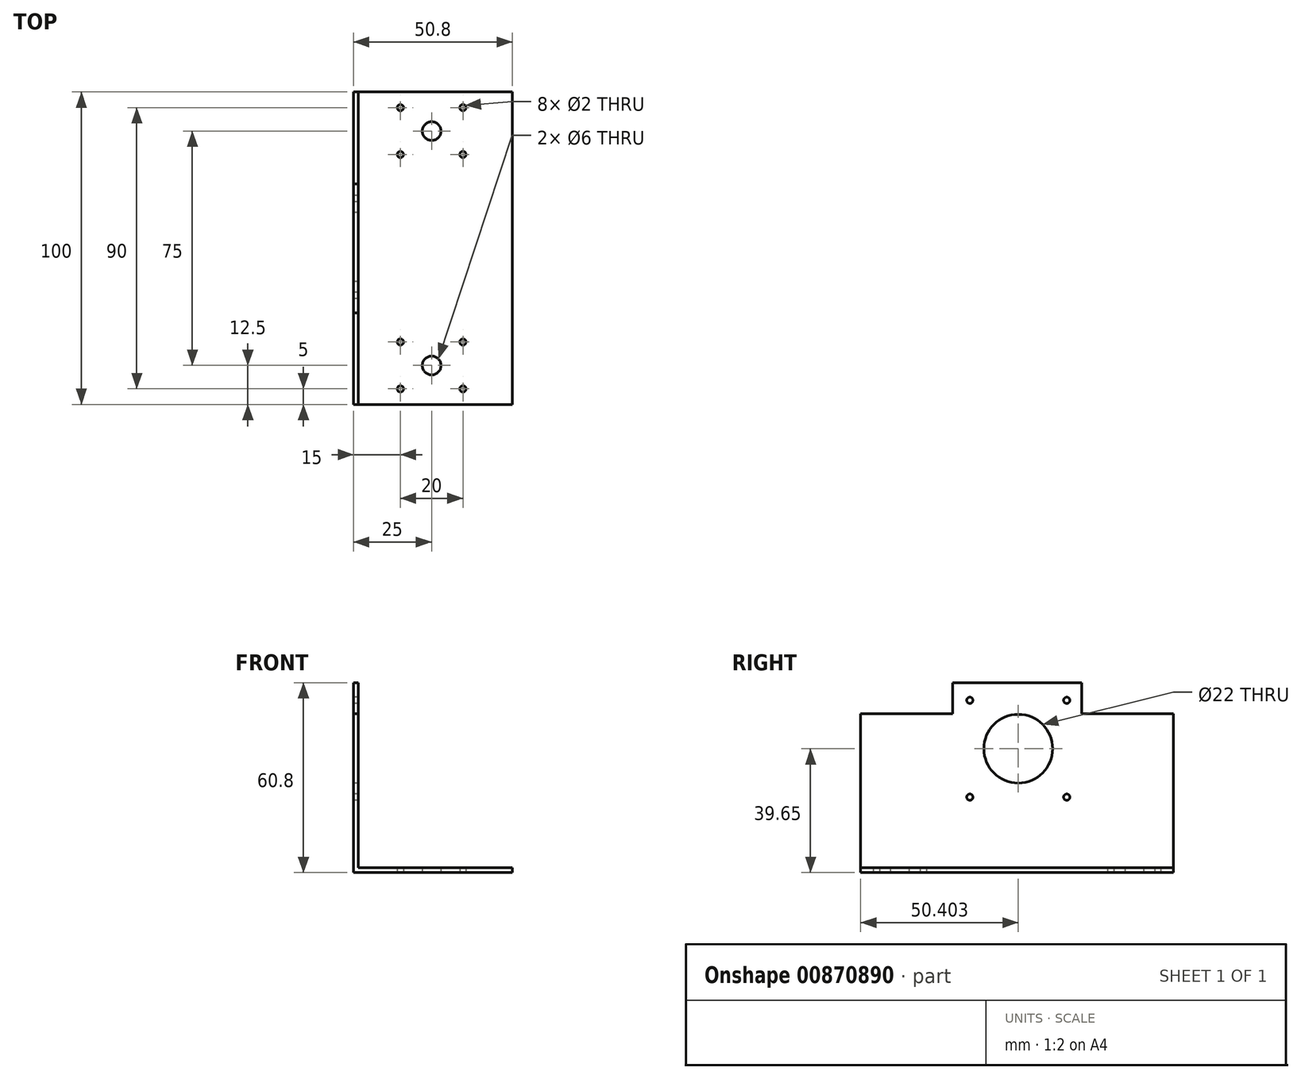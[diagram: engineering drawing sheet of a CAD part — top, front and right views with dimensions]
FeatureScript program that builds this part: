
annotation { "Feature Type Name" : "Feature", "Feature Type Description" : "" }
export const myFeature = defineFeature(function(context is Context, id is Id, definition is map)
    precondition{}
    {
        {
            var Q0;
            Q0=qCreatedBy(makeId("Front.planeOp"),FACE);
            var sketch = newSketch(context, id + "F0", { "sketchPlane" : qUnion([Q0])});
            skLineSegment(sketch, "E0", {"start": v(0, 0) * mm, "end": v(0, 50.8) * mm});
            skLineSegment(sketch, "E1", {"start": v(0, 50.8) * mm, "end": v(1.59, 50.8) * mm});
            skLineSegment(sketch, "E2", {"start": v(1.59, 50.8) * mm, "end": v(1.6, 1.59) * mm});
            skLineSegment(sketch, "E3", {"start": v(1.6, 1.59) * mm, "end": v(50.8, 1.6) * mm});
            skLineSegment(sketch, "E4", {"start": v(50.8, 1.6) * mm, "end": v(50.8, 0) * mm});
            skLineSegment(sketch, "E5", {"start": v(50.8, 0) * mm, "end": v(0, 0) * mm});
            skSolve(sketch);
        }
        {
            var Q0;
            Q0=qSketchRegion(id+"F0",true);
            extrude(context, id + "F1", {"entities" : qUnion([Q0]), "depth" : 100 * mm, "offsetDistance" : 25 * mm});
        }
        {
            var Q0;
            Q0=qCreatedBy(makeId("Top.planeOp"),FACE);
            var sketch = newSketch(context, id + "F2", { "sketchPlane" : qUnion([Q0])});
            skCircle(sketch, "E6", {"center": v(15, -5) * mm, "radius": 1 * mm});
            skCircle(sketch, "E7", {"center": v(35, -5) * mm, "radius": 1 * mm});
            skCircle(sketch, "E8", {"center": v(15, -20) * mm, "radius": 1 * mm});
            skCircle(sketch, "E9", {"center": v(35, -20) * mm, "radius": 1 * mm});
            skPoint(sketch, "E10", {"position": v(35, -80) * mm});
            skPoint(sketch, "E11", {"position": v(35, -95) * mm});
            skPoint(sketch, "E12", {"position": v(15, -80) * mm});
            skPoint(sketch, "E13", {"position": v(15, -95) * mm});
            skCircle(sketch, "E14", {"center": v(35, -80) * mm, "radius": 1 * mm});
            skCircle(sketch, "E15", {"center": v(15, -80) * mm, "radius": 1 * mm});
            skCircle(sketch, "E16", {"center": v(35, -95) * mm, "radius": 1 * mm});
            skCircle(sketch, "E17", {"center": v(15, -95) * mm, "radius": 1 * mm});
            skPoint(sketch, "E18", {"position": v(25, -12.5) * mm});
            skPoint(sketch, "E19", {"position": v(25, -87.5) * mm});
            skCircle(sketch, "E20", {"center": v(25, -87.5) * mm, "radius": 3 * mm});
            skCircle(sketch, "E21", {"center": v(25, -12.5) * mm, "radius": 3 * mm});
            skSolve(sketch);
        }
        {
            var Q0;
            Q0=qSketchRegion(id+"F2",true);
            extrude(context, id + "F3", {"entities" : qUnion([Q0]), "operationType" : NewBodyOperationType.REMOVE, "endBound" : BoundingType.THROUGH_ALL, "depth" : 25 * mm, "offsetDistance" : 25 * mm});
        }
        {
            var Q0;
            Q0=qCreatedBy(makeId("Right.planeOp"),FACE);
            var sketch = newSketch(context, id + "F4", { "sketchPlane" : qUnion([Q0])});
            skPoint(sketch, "E22", {"position": v(-50, 50.8) * mm});
            skLineSegment(sketch, "E23", {"start": v(-70.65, 50.8) * mm, "end": v(-29.35, 50.8) * mm});
            skLineSegment(sketch, "E24", {"start": v(-70.65, 50.8) * mm, "end": v(-70.65, 60.8) * mm});
            skLineSegment(sketch, "E25", {"start": v(-29.35, 50.8) * mm, "end": v(-29.35, 60.8) * mm});
            skLineSegment(sketch, "E26", {"start": v(-29.35, 60.8) * mm, "end": v(-70.65, 60.8) * mm});
            skSolve(sketch);
        }
        {
            var Q0;
            Q0 = qSketchRegion(id + "F4", true);
            extrude(context, id + "F5", {"entities" : qUnion([Q0]), "operationType" : NewBodyOperationType.ADD, "depth" : 1.59 * mm, "offsetDistance" : 25 * mm});
        }
        {
            var Q0;
            Q0=qCreatedBy(makeId("Right.planeOp"),FACE);
            var sketch = newSketch(context, id + "F6", { "sketchPlane" : qUnion([Q0])});
            skPoint(sketch, "E27", {"position": v(-49.6, 39.65) * mm});
            skPoint(sketch, "E28", {"position": v(-65.1, 24.15) * mm});
            skPoint(sketch, "E29", {"position": v(-34.1, 24.15) * mm});
            skPoint(sketch, "E30", {"position": v(-34.1, 55.15) * mm});
            skPoint(sketch, "E31", {"position": v(-65.1, 55.15) * mm});
            skCircle(sketch, "E32", {"center": v(-65.1, 24.15) * mm, "radius": 1 * mm});
            skCircle(sketch, "E33", {"center": v(-34.1, 24.15) * mm, "radius": 1 * mm});
            skCircle(sketch, "E34", {"center": v(-34.1, 55.15) * mm, "radius": 1 * mm});
            skCircle(sketch, "E35", {"center": v(-65.1, 55.15) * mm, "radius": 1 * mm});
            skCircle(sketch, "E36", {"center": v(-49.6, 39.65) * mm, "radius": 11 * mm});
            skSolve(sketch);
        }
        {
            var Q0;
            Q0 = qSketchRegion(id + "F6", true);
            extrude(context, id + "F7", {"entities" : qUnion([Q0]), "operationType" : NewBodyOperationType.REMOVE, "endBound" : BoundingType.THROUGH_ALL, "depth" : 25 * mm, "offsetDistance" : 25 * mm});
        }
    });
